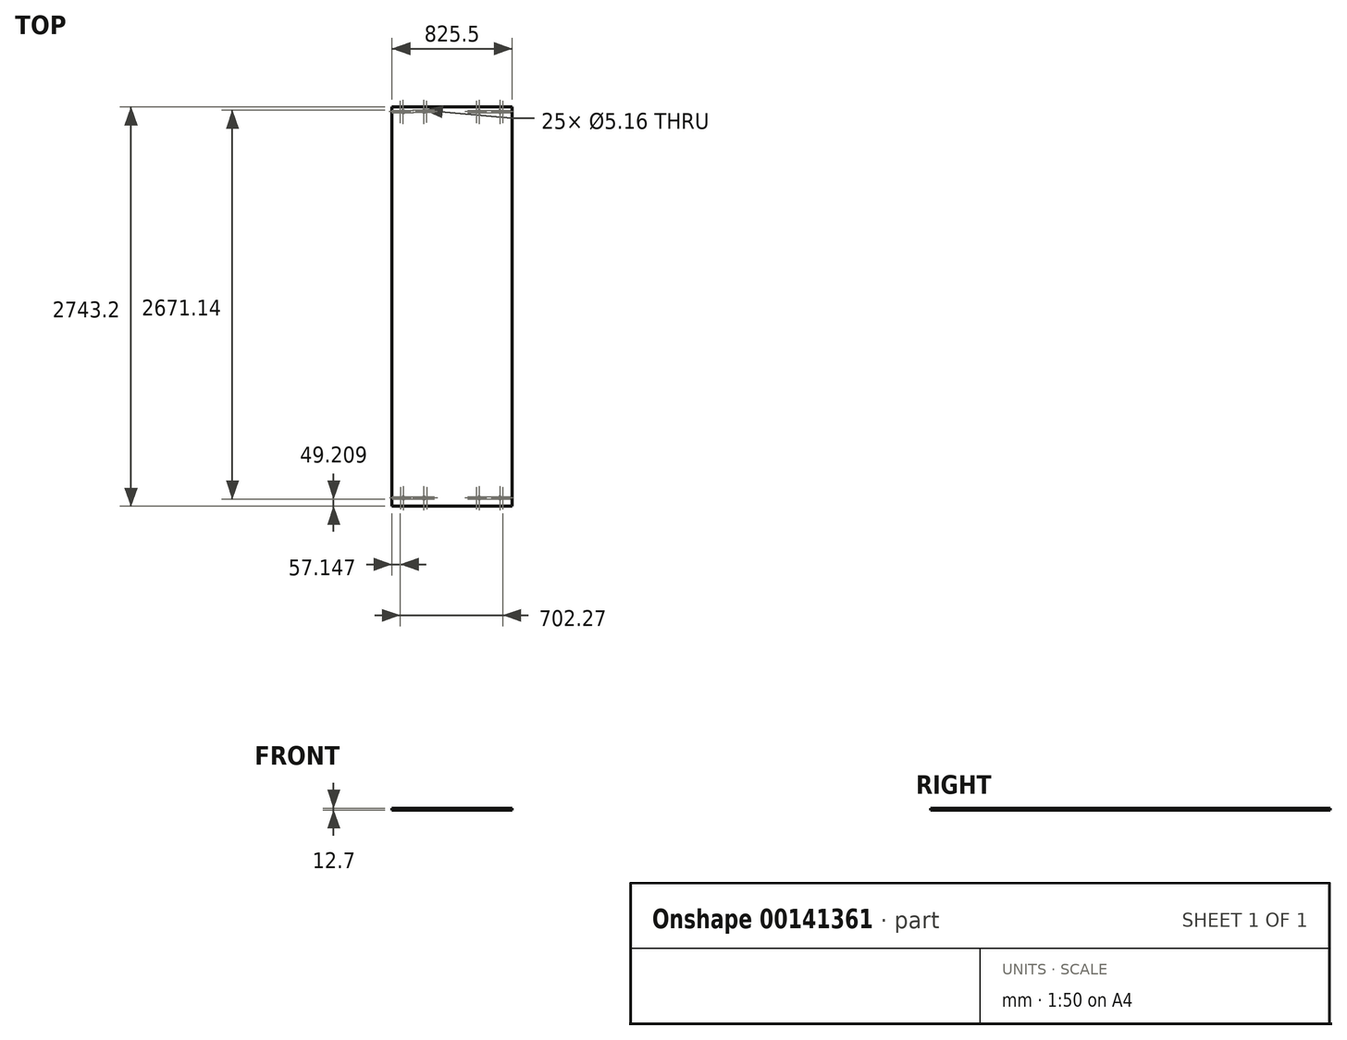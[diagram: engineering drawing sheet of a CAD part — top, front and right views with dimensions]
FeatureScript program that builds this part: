
annotation { "Feature Type Name" : "Feature", "Feature Type Description" : "" }
export const myFeature = defineFeature(function(context is Context, id is Id, definition is map)
    precondition{}
    {
        {
            var Q0;
            Q0=qCreatedBy(makeId("Top.planeOp"),FACE);
            var sketch = newSketch(context, id + "F0", { "sketchPlane" : qUnion([Q0])});
            skLineSegment(sketch, "E0.bottom", {"start": v(-1246.62, 2708.73) * mm, "end": v(-421.12, 2708.73) * mm});
            skLineSegment(sketch, "E0.top", {"start": v(-1246.62, -34.47) * mm, "end": v(-421.12, -34.47) * mm});
            skLineSegment(sketch, "E0.left", {"start": v(-1246.62, 2708.73) * mm, "end": v(-1246.62, -34.47) * mm});
            skLineSegment(sketch, "E0.right", {"start": v(-421.12, 2708.73) * mm, "end": v(-421.12, -34.47) * mm});
            skSolve(sketch);
        }
        {
            var Q0;
            Q0 = qSketchRegion(id + "F0", true);
            extrude(context, id + "F1", {"entities" : qUnion([Q0]), "depth" : 12.7 * mm});
        }
        {
            var Q0;
            Q0=makeQuery(id+"F1.opExtrude","CAP_FACE",FACE,{"disambiguationData":[OSD([sQuery(id+"F0.wireOp",EDGE,"E0.bottom"),sQuery(id+"F0.wireOp",EDGE,"E0.top"),sQuery(id+"F0.wireOp",EDGE,"E0.left"),sQuery(id+"F0.wireOp",EDGE,"E0.right")])],"isStart":false});
            var sketch = newSketch(context, id + "F2", { "sketchPlane" : qUnion([Q0])});
            skCircle(sketch, "E1", {"center": v(-487.2, 22.68) * mm, "radius": 2.58 * mm});
            skCircle(sketch, "E2", {"center": v(-668.18, 22.68) * mm, "radius": 2.58 * mm});
            skCircle(sketch, "E3", {"center": v(-1186.9, 22.68) * mm, "radius": 2.58 * mm});
            skCircle(sketch, "E4", {"center": v(-506.25, 30.61) * mm, "radius": 2.58 * mm});
            skCircle(sketch, "E5", {"center": v(-506.25, 14.74) * mm, "radius": 2.58 * mm});
            skCircle(sketch, "E6", {"center": v(-649.13, 30.61) * mm, "radius": 2.58 * mm});
            skCircle(sketch, "E7", {"center": v(-649.13, 14.74) * mm, "radius": 2.58 * mm});
            skCircle(sketch, "E8", {"center": v(-1167.84, 30.61) * mm, "radius": 2.58 * mm});
            skCircle(sketch, "E9", {"center": v(-1167.84, 14.74) * mm, "radius": 2.58 * mm});
            skLineSegment(sketch, "E10", {"start": v(-1005.92, 22.68) * mm, "end": v(-1027.55, 22.68) * mm});
            skLineSegment(sketch, "E11", {"start": v(-1027.55, 30.61) * mm, "end": v(-1027.55, 14.74) * mm});
            skCircle(sketch, "E12", {"center": v(-1027.55, 30.61) * mm, "radius": 2.58 * mm});
            skCircle(sketch, "E13", {"center": v(-1027.55, 14.74) * mm, "radius": 2.58 * mm});
            skCircle(sketch, "E14", {"center": v(-1005.92, 22.68) * mm, "radius": 2.58 * mm});
            skCircle(sketch, "E15", {"center": v(-1170.42, 2685.03) * mm, "radius": 2.58 * mm});
            skCircle(sketch, "E16", {"center": v(-1170.42, 2669.15) * mm, "radius": 2.58 * mm});
            skCircle(sketch, "E17", {"center": v(-1189.47, 2676.98) * mm, "radius": 2.58 * mm});
            skCircle(sketch, "E18", {"center": v(-1027.55, 2685.88) * mm, "radius": 2.58 * mm});
            skCircle(sketch, "E19", {"center": v(-1027.55, 2670) * mm, "radius": 2.58 * mm});
            skCircle(sketch, "E20", {"center": v(-1008.5, 2678.05) * mm, "radius": 2.58 * mm});
            skCircle(sketch, "E21", {"center": v(-668.18, 2676.98) * mm, "radius": 2.58 * mm});
            skCircle(sketch, "E22", {"center": v(-649.13, 2684.91) * mm, "radius": 2.58 * mm});
            skCircle(sketch, "E23", {"center": v(-649.13, 2669.04) * mm, "radius": 2.58 * mm});
            skCircle(sketch, "E24", {"center": v(-487.2, 2676.98) * mm, "radius": 2.58 * mm});
            skCircle(sketch, "E25", {"center": v(-506.25, 2684.91) * mm, "radius": 2.58 * mm});
            skCircle(sketch, "E26", {"center": v(-506.25, 2669.04) * mm, "radius": 2.58 * mm});
            skSolve(sketch);
        }
        {
            var Q0;
            Q0=sQuery(id+"F2.wireOp",VERTEX,"E24.center");
            var Q1;
            Q1=sQuery(id+"F2.wireOp",VERTEX,"E21.center");
            var Q2;
            Q2=sQuery(id+"F2.wireOp",VERTEX,"E22.center");
            var Q3;
            Q3=sQuery(id+"F2.wireOp",VERTEX,"E17.center");
            var Q4;
            Q4=sQuery(id+"F2.wireOp",VERTEX,"E19.center");
            var Q5;
            Q5=sQuery(id+"F2.wireOp",VERTEX,"E18.center");
            var Q6;
            Q6=sQuery(id+"F2.wireOp",VERTEX,"E25.center");
            var Q7;
            Q7=sQuery(id+"F2.wireOp",VERTEX,"E20.center");
            var Q8;
            Q8=sQuery(id+"F2.wireOp",VERTEX,"E15.center");
            var Q9;
            Q9=sQuery(id+"F2.wireOp",VERTEX,"E23.center");
            var Q10;
            Q10=sQuery(id+"F2.wireOp",VERTEX,"E16.center");
            var Q11;
            Q11=sQuery(id+"F2.wireOp",VERTEX,"E26.center");
            var Q12;
            Q12=sQuery(id+"F2.wireOp",VERTEX,"E14.center");
            var Q13;
            Q13=sQuery(id+"F2.wireOp",VERTEX,"E13.center");
            var Q14;
            Q14=sQuery(id+"F2.wireOp",VERTEX,"E9.center");
            var Q15;
            Q15=sQuery(id+"F2.wireOp",VERTEX,"E2.center");
            var Q16;
            Q16=sQuery(id+"F2.wireOp",VERTEX,"E7.center");
            var Q17;
            Q17=sQuery(id+"F2.wireOp",VERTEX,"E12.center");
            var Q18;
            Q18=sQuery(id+"F2.wireOp",VERTEX,"E6.center");
            var Q19;
            Q19=sQuery(id+"F2.wireOp",VERTEX,"E5.center");
            var Q20;
            Q20=sQuery(id+"F2.wireOp",VERTEX,"E8.center");
            var Q21;
            Q21=sQuery(id+"F2.wireOp",VERTEX,"E3.center");
            var Q22;
            Q22=sQuery(id+"F2.wireOp",VERTEX,"E4.center");
            var Q23;
            Q23=sQuery(id+"F2.wireOp",VERTEX,"E1.center");
            var Q24;
            Q24=sQuery(id+"F2.wireOp",VERTEX,"E10.end");
            var Q25;
            Q25=makeQuery(id+"F1.opExtrude","SWEPT_BODY",BODY,{"disambiguationData":[OSD([sQuery(id+"F0.wireOp",EDGE,"E0.bottom"),sQuery(id+"F0.wireOp",EDGE,"E0.top"),sQuery(id+"F0.wireOp",EDGE,"E0.left"),sQuery(id+"F0.wireOp",EDGE,"E0.right")])]});
            hole(context, id + "F3", {"style" : HoleStyle.SIMPLE, "endStyle" : HoleEndStyle.THROUGH, "holeDiameter" : 5.16 * mm, "locations" : qUnion([Q0, Q1, Q2, Q3, Q4, Q5, Q6, Q7, Q8, Q9, Q10, Q11, Q12, Q13, Q14, Q15, Q16, Q17, Q18, Q19, Q20, Q21, Q22, Q23, Q24]), "scope" : qUnion([Q25]), "isTappedThrough" : true});
        }
    });
